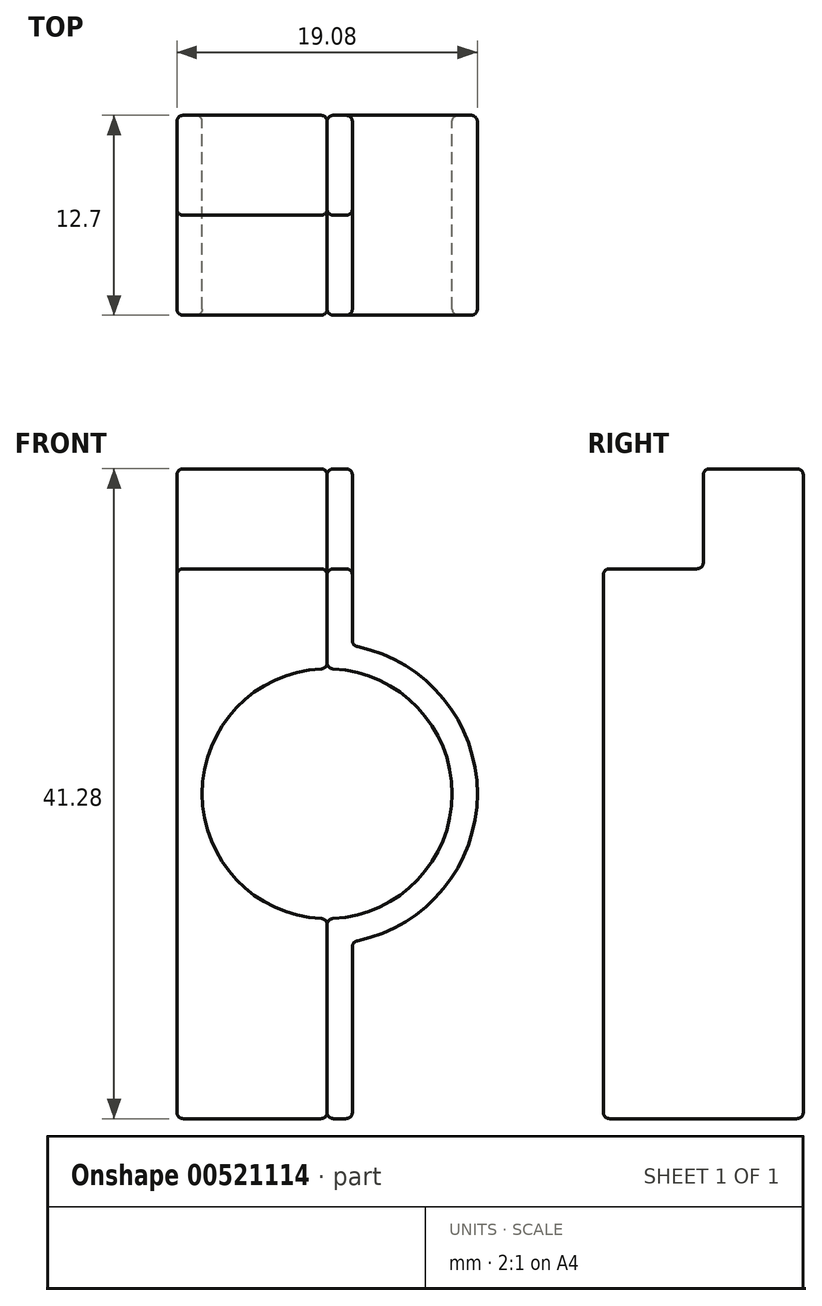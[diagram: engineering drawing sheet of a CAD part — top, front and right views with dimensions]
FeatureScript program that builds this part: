
annotation { "Feature Type Name" : "Feature", "Feature Type Description" : "" }
export const myFeature = defineFeature(function(context is Context, id is Id, definition is map)
    precondition{}
    {
        {
            var Q0;
            Q0=qCreatedBy(makeId("Front.planeOp"),FACE);
            var sketch = newSketch(context, id + "F0", { "sketchPlane" : qUnion([Q0])});
            skArc(sketch, "E0", {"start": v(0, -7.94) * mm, "mid": v(7.94, 0) * mm, "end": v(0, 7.94) * mm});
            skArc(sketch, "E1", {"start": v(1.6, -9.4) * mm, "mid": v(9.54, 0) * mm, "end": v(1.6, 9.4) * mm});
            skLineSegment(sketch, "E2.top", {"start": v(0, 20.64) * mm, "end": v(1.6, 20.64) * mm});
            skLineSegment(sketch, "E2.left", {"start": v(0, 7.94) * mm, "end": v(0, 20.64) * mm});
            skLineSegment(sketch, "E2.right", {"start": v(1.6, 9.4) * mm, "end": v(1.6, 20.64) * mm});
            skLineSegment(sketch, "E3", {"start": v(0, 0) * mm, "end": v(1.73, 0) * mm, "construction": true});
            skLineSegment(sketch, "E4.MirrorCS", {"start": v(1.6, -9.4) * mm, "end": v(1.6, -20.64) * mm});
            skLineSegment(sketch, "E5.MirrorCS", {"start": v(0, -7.94) * mm, "end": v(0, -20.64) * mm});
            skLineSegment(sketch, "E6.MirrorCS", {"start": v(0, -20.64) * mm, "end": v(1.6, -20.64) * mm});
            skLineSegment(sketch, "E7", {"start": v(0, 0) * mm, "end": v(0, 3.25) * mm, "construction": true});
            skArc(sketch, "E8.MirrorCS", {"start": v(0, -7.94) * mm, "mid": v(-7.94, 0) * mm, "end": v(0, 7.94) * mm});
            skLineSegment(sketch, "E9.MirrorCS", {"start": v(0, -20.64) * mm, "end": v(-1.6, -20.64) * mm});
            skLineSegment(sketch, "E10.MirrorCS", {"start": v(0, 20.64) * mm, "end": v(-1.6, 20.64) * mm});
            skLineSegment(sketch, "E11.bottom", {"start": v(-1.6, -20.64) * mm, "end": v(-9.54, -20.64) * mm});
            skLineSegment(sketch, "E11.right", {"start": v(-9.54, -20.64) * mm, "end": v(-9.54, 0) * mm});
            skLineSegment(sketch, "E12.MirrorCS", {"start": v(-1.6, 20.64) * mm, "end": v(-9.54, 20.64) * mm});
            skLineSegment(sketch, "E13.MirrorCS", {"start": v(-9.54, 20.64) * mm, "end": v(-9.54, 0) * mm});
            skPoint(sketch, "E14.orphan", {"position": v(-1.6, -9.4) * mm});
            skPoint(sketch, "E15.MirrorCS.end.orphan", {"position": v(-1.6, 9.4) * mm});
            skPoint(sketch, "E16.MirrorCS.end.orphan", {"position": v(-1.6, 20.64) * mm});
            skSolve(sketch);
        }
        {
            var Q0;
            Q0=makeQuery(id+"F0.imprint","IMPRINT",FACE,{"disambiguationData":[TD([[makeQuery(id+"F0.imprint","IMPRINT",EDGE,{"derivedFrom":sQuery(id+"F0.wireOp",EDGE,"E0")}),-1.0]])]});
            extrude(context, id + "F1", {"entities" : qUnion([Q0]), "depth" : 12.7 * mm, "offsetDistance" : 25.4 * mm});
        }
        {
            var Q0;
            Q0=makeQuery(id+"F1.opExtrude","SWEPT_EDGE",EDGE,{"disambiguationData":[OSD([sQuery(id+"F0.wireOp",EDGE,"E1"),sQuery(id+"F0.wireOp",EDGE,"E2.right")])]});
            var Q1;
            Q1=makeQuery(id+"F1.opExtrude","SWEPT_EDGE",EDGE,{"disambiguationData":[OSD([sQuery(id+"F0.wireOp",EDGE,"E1"),sQuery(id+"F0.wireOp",EDGE,"E4.MirrorCS")])]});
            var Q2;
            Q2=makeQuery(id+"F1.opExtrude","SWEPT_EDGE",EDGE,{"disambiguationData":[OSD([sQuery(id+"F0.wireOp",EDGE,"E0"),sQuery(id+"F0.wireOp",EDGE,"E2.left")])]});
            var Q3;
            Q3=makeQuery(id+"F1.opExtrude","SWEPT_EDGE",EDGE,{"disambiguationData":[OSD([sQuery(id+"F0.wireOp",EDGE,"E0"),sQuery(id+"F0.wireOp",EDGE,"E5.MirrorCS")])]});
            var Q4;
            Q4=makeQuery(id+"F1.opExtrude","CAP_FACE",FACE,{"disambiguationData":[OSD([sQuery(id+"F0.wireOp",EDGE,"E0"),sQuery(id+"F0.wireOp",EDGE,"E1"),sQuery(id+"F0.wireOp",EDGE,"E2.top"),sQuery(id+"F0.wireOp",EDGE,"E2.left"),sQuery(id+"F0.wireOp",EDGE,"E2.right"),sQuery(id+"F0.wireOp",EDGE,"E4.MirrorCS"),sQuery(id+"F0.wireOp",EDGE,"E5.MirrorCS"),sQuery(id+"F0.wireOp",EDGE,"E6.MirrorCS")])],"isStart":true});
            var Q5;
            Q5=makeQuery(id+"F1.opExtrude","CAP_FACE",FACE,{"disambiguationData":[OSD([sQuery(id+"F0.wireOp",EDGE,"E0"),sQuery(id+"F0.wireOp",EDGE,"E1"),sQuery(id+"F0.wireOp",EDGE,"E2.top"),sQuery(id+"F0.wireOp",EDGE,"E2.left"),sQuery(id+"F0.wireOp",EDGE,"E2.right"),sQuery(id+"F0.wireOp",EDGE,"E4.MirrorCS"),sQuery(id+"F0.wireOp",EDGE,"E5.MirrorCS"),sQuery(id+"F0.wireOp",EDGE,"E6.MirrorCS")])],"isStart":false});
            var Q6;
            Q6=makeQuery(id+"F1.opExtrude","SWEPT_FACE",FACE,{"disambiguationData":[OSD([sQuery(id+"F0.wireOp",EDGE,"E6.MirrorCS")])]});
            var Q7;
            Q7=makeQuery(id+"F1.opExtrude","SWEPT_FACE",FACE,{"disambiguationData":[OSD([sQuery(id+"F0.wireOp",EDGE,"E2.top")])]});
            fillet(context, id + "F2", {"entities" : qUnion([Q0, Q1, Q2, Q3, Q4, Q5, Q6, Q7]), "radius" : 0.4 * mm, "tangentPropagation" : true, "allowEdgeOverflow" : false});
        }
        {
            var Q0;
            Q0=makeQuery(id+"F0.imprint","IMPRINT",FACE,{"disambiguationData":[TD([[makeQuery(id+"F0.imprint","IMPRINT",EDGE,{"derivedFrom":sQuery(id+"F0.wireOp",EDGE,"E5.MirrorCS")}),-1.0]])]});
            extrude(context, id + "F3", {"entities" : qUnion([Q0]), "depth" : 12.7 * mm, "offsetDistance" : 25.4 * mm});
        }
        {
            var Q0;
            Q0=makeQuery(id+"F3.opExtrude","SWEPT_FACE",FACE,{"disambiguationData":[OSD([sQuery(id+"F0.wireOp",EDGE,"E11.right"),sQuery(id+"F0.wireOp",EDGE,"E13.MirrorCS")])]});
            var sketch = newSketch(context, id + "F4", { "sketchPlane" : qUnion([Q0])});
            skLineSegment(sketch, "E17.bottom", {"start": v(12.7, 20.64) * mm, "end": v(6.35, 20.64) * mm});
            skLineSegment(sketch, "E17.top", {"start": v(12.7, 14.29) * mm, "end": v(6.35, 14.29) * mm});
            skLineSegment(sketch, "E17.left", {"start": v(12.7, 20.64) * mm, "end": v(12.7, 14.29) * mm});
            skLineSegment(sketch, "E17.right", {"start": v(6.35, 20.64) * mm, "end": v(6.35, 14.29) * mm});
            skSolve(sketch);
        }
        {
            var Q0;
            Q0 = qSketchRegion(id + "F4", true);
            extrude(context, id + "F5", {"entities" : qUnion([Q0]), "operationType" : NewBodyOperationType.REMOVE, "oppositeDirection" : true, "depth" : 25.4 * mm, "offsetDistance" : 25.4 * mm});
        }
        {
            var Q0;
            Q0=makeQuery(id+"F3.opExtrude","SWEPT_FACE",FACE,{"disambiguationData":[OSD([sQuery(id+"F0.wireOp",EDGE,"E8.MirrorCS")])]});
            var Q1;
            Q1=makeQuery(id+"F3.opExtrude","CAP_FACE",FACE,{"disambiguationData":[OSD([sQuery(id+"F0.wireOp",EDGE,"E5.MirrorCS"),sQuery(id+"F0.wireOp",EDGE,"E2.left"),sQuery(id+"F0.wireOp",EDGE,"E8.MirrorCS"),sQuery(id+"F0.wireOp",EDGE,"E9.MirrorCS"),sQuery(id+"F0.wireOp",EDGE,"E10.MirrorCS"),sQuery(id+"F0.wireOp",EDGE,"E11.bottom"),sQuery(id+"F0.wireOp",EDGE,"E11.right"),sQuery(id+"F0.wireOp",EDGE,"E12.MirrorCS"),sQuery(id+"F0.wireOp",EDGE,"E13.MirrorCS")])],"isStart":true});
            var Q2;
            Q2=makeQuery(id+"F3.opExtrude","CAP_FACE",FACE,{"disambiguationData":[OSD([sQuery(id+"F0.wireOp",EDGE,"E5.MirrorCS"),sQuery(id+"F0.wireOp",EDGE,"E2.left"),sQuery(id+"F0.wireOp",EDGE,"E8.MirrorCS"),sQuery(id+"F0.wireOp",EDGE,"E9.MirrorCS"),sQuery(id+"F0.wireOp",EDGE,"E10.MirrorCS"),sQuery(id+"F0.wireOp",EDGE,"E11.bottom"),sQuery(id+"F0.wireOp",EDGE,"E11.right"),sQuery(id+"F0.wireOp",EDGE,"E12.MirrorCS"),sQuery(id+"F0.wireOp",EDGE,"E13.MirrorCS")])],"isStart":false});
            var Q3;
            Q3=makeQuery(id+"F3.opExtrude","SWEPT_FACE",FACE,{"disambiguationData":[OSD([sQuery(id+"F0.wireOp",EDGE,"E10.MirrorCS"),sQuery(id+"F0.wireOp",EDGE,"E12.MirrorCS")])]});
            var Q4;
            Q4=makeQuery(id+"F3.opExtrude","SWEPT_FACE",FACE,{"disambiguationData":[OSD([sQuery(id+"F0.wireOp",EDGE,"E9.MirrorCS"),sQuery(id+"F0.wireOp",EDGE,"E11.bottom")])]});
            var Q5;
            Q5=makeQuery(id+"F5.boolean.opBoolean","COPY",FACE,{"derivedFrom":makeQuery(id+"F5.opExtrude","SWEPT_FACE",FACE,{"disambiguationData":[OSD([sQuery(id+"F4.wireOp",EDGE,"E17.right")])]})});
            var Q6;
            Q6=makeQuery(id+"F5.boolean.opBoolean","COPY",FACE,{"derivedFrom":makeQuery(id+"F5.opExtrude","SWEPT_FACE",FACE,{"disambiguationData":[OSD([sQuery(id+"F4.wireOp",EDGE,"E17.top")])]})});
            fillet(context, id + "F6", {"entities" : qUnion([Q0, Q1, Q2, Q3, Q4, Q5, Q6]), "radius" : 0.4 * mm, "tangentPropagation" : true, "allowEdgeOverflow" : false});
        }
    });
